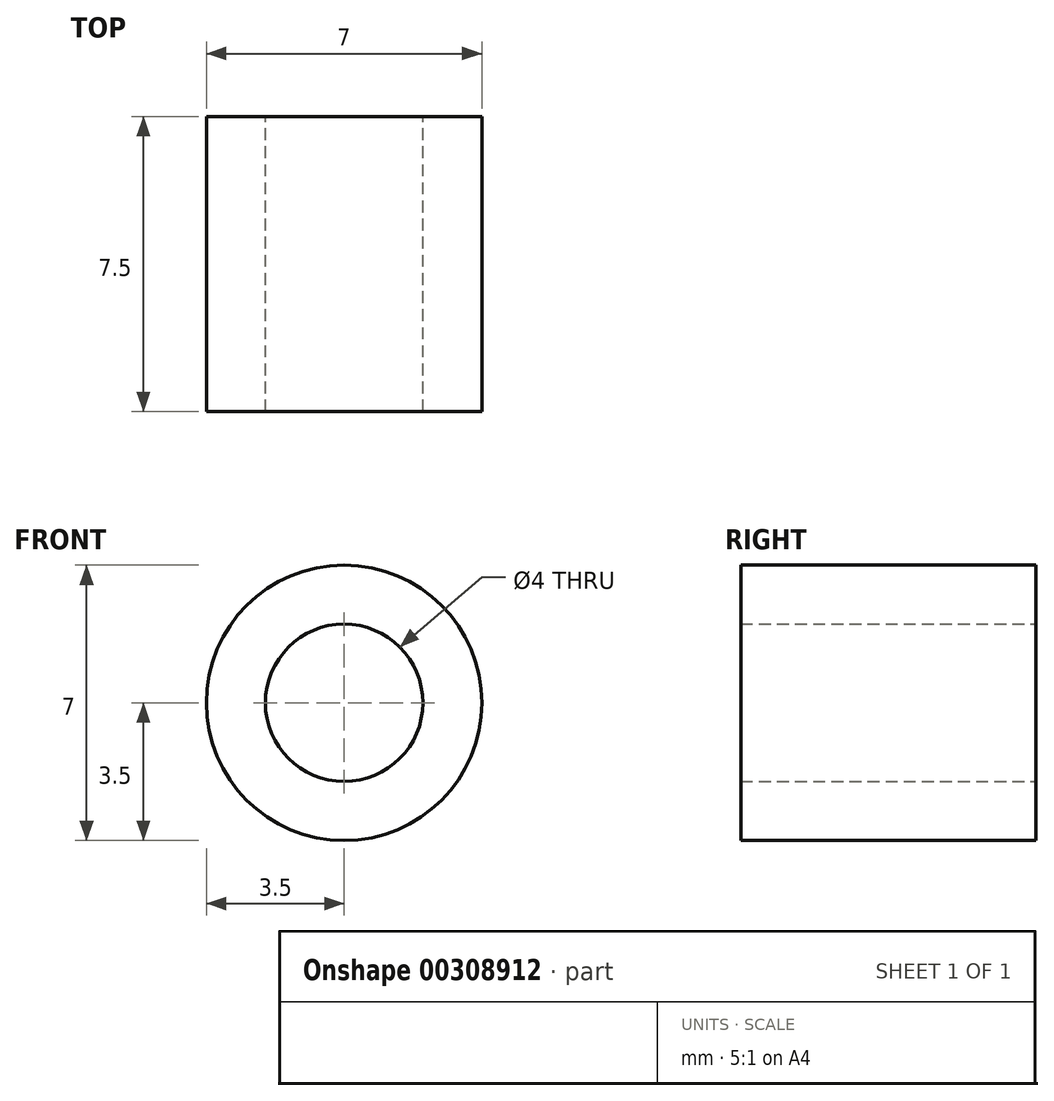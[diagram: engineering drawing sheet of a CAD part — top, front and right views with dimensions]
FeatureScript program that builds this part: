
annotation { "Feature Type Name" : "Feature", "Feature Type Description" : "" }
export const myFeature = defineFeature(function(context is Context, id is Id, definition is map)
    precondition{}
    {
        {
            var Q0;
            Q0=qCreatedBy(makeId("Front.planeOp"),FACE);
            var sketch = newSketch(context, id + "F0", { "sketchPlane" : qUnion([Q0])});
            skCircle(sketch, "E0", {"center": v(0, 0) * mm, "radius": 3.5 * mm});
            skCircle(sketch, "E1", {"center": v(0, 0) * mm, "radius": 2 * mm});
            skSolve(sketch);
        }
        {
            var Q0;
            Q0 = qSketchRegion(id + "F0", true);
            extrude(context, id + "F1", {"entities" : qUnion([Q0]), "depth" : 7.5 * mm});
        }
    });
